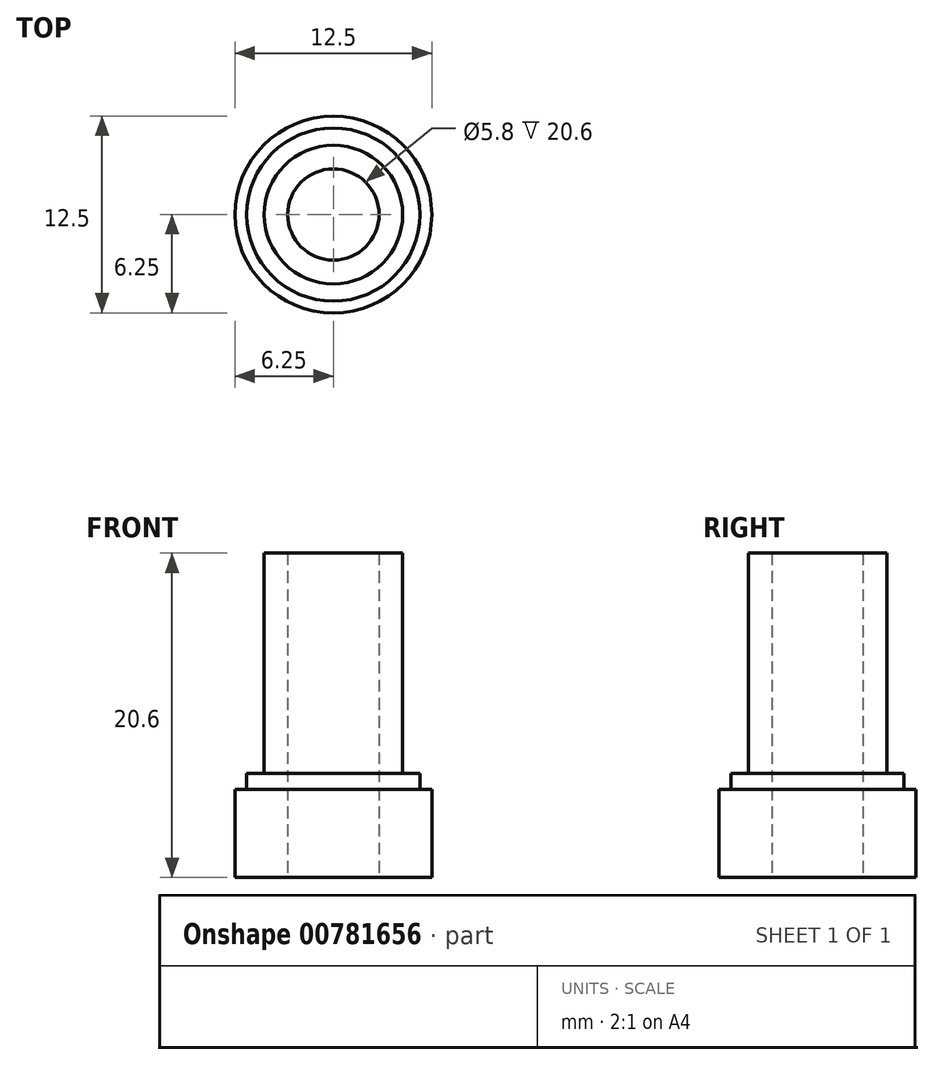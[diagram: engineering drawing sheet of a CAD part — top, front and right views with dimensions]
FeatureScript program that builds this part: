
annotation { "Feature Type Name" : "Feature", "Feature Type Description" : "" }
export const myFeature = defineFeature(function(context is Context, id is Id, definition is map)
    precondition{}
    {
        {
            assignVariable(context, id + "F0", {"name" : "h0", "anyValue" : 5.6});
        }
        {
            assignVariable(context, id + "F1", {"name" : "h1", "anyValue" : 6.6});
        }
        {
            assignVariable(context, id + "F2", {"name" : "h2", "anyValue" : 20.6});
        }
        {
            var Q0;
            Q0=qCreatedBy(makeId("Top.planeOp"),FACE);
            var sketch = newSketch(context, id + "F3", { "sketchPlane" : qUnion([Q0])});
            skCircle(sketch, "E0", {"center": v(0, 0) * mm, "radius": 2.9 * mm});
            skCircle(sketch, "E1", {"center": v(0, 0) * mm, "radius": 6.25 * mm});
            skSolve(sketch);
        }
        {
            var Q0;
            Q0=makeQuery(id+"F3.imprint","IMPRINT",FACE,{"disambiguationData":[TD([[makeQuery(id+"F3.imprint","IMPRINT",EDGE,{"derivedFrom":sQuery(id+"F3.wireOp",EDGE,"E0")}),-1.0]])]});
            extrude(context, id + "F4", {"entities" : qUnion([Q0]), "depth" : (getVariable(context, 'h0')) * mm, "offsetDistance" : 25 * mm});
        }
        {
            var Q0;
            Q0=makeQuery(id+"F4.opExtrude","CAP_FACE",FACE,{"disambiguationData":[OSD([sQuery(id+"F3.wireOp",EDGE,"E0"),sQuery(id+"F3.wireOp",EDGE,"E1")])],"isStart":false});
            var sketch = newSketch(context, id + "F5", { "sketchPlane" : qUnion([Q0])});
            skCircle(sketch, "E2", {"center": v(0, 0) * mm, "radius": 5.5 * mm});
            skCircle(sketch, "E3", {"center": v(0, 0) * mm, "radius": 2.9 * mm});
            skSolve(sketch);
        }
        {
            var Q0;
            Q0=makeQuery(id+"F5.imprint","IMPRINT",FACE,{"disambiguationData":[TD([[makeQuery(id+"F5.imprint","IMPRINT",EDGE,{"derivedFrom":sQuery(id+"F5.wireOp",EDGE,"E2")}),1.0]])]});
            extrude(context, id + "F6", {"entities" : qUnion([Q0]), "operationType" : NewBodyOperationType.ADD, "depth" : (getVariable(context, 'h1') - getVariable(context, 'h0')) * mm, "offsetDistance" : 25 * mm});
        }
        {
            var Q0;
            Q0=makeQuery(id+"F6.opExtrude","CAP_FACE",FACE,{"disambiguationData":[OSD([sQuery(id+"F5.wireOp",EDGE,"E2"),sQuery(id+"F5.wireOp",EDGE,"E3")])],"isStart":false});
            var sketch = newSketch(context, id + "F7", { "sketchPlane" : qUnion([Q0])});
            skCircle(sketch, "E4", {"center": v(0, 0) * mm, "radius": 2.9 * mm});
            skCircle(sketch, "E5", {"center": v(0, 0) * mm, "radius": 4.4 * mm});
            skSolve(sketch);
        }
        {
            var Q0;
            Q0=makeQuery(id+"F7.imprint","IMPRINT",FACE,{"disambiguationData":[TD([[makeQuery(id+"F7.imprint","IMPRINT",EDGE,{"derivedFrom":sQuery(id+"F7.wireOp",EDGE,"E4")}),-1.0]])]});
            extrude(context, id + "F8", {"entities" : qUnion([Q0]), "operationType" : NewBodyOperationType.ADD, "depth" : (getVariable(context, 'h2') - getVariable(context, 'h1')) * mm, "offsetDistance" : 25 * mm});
        }
    });
